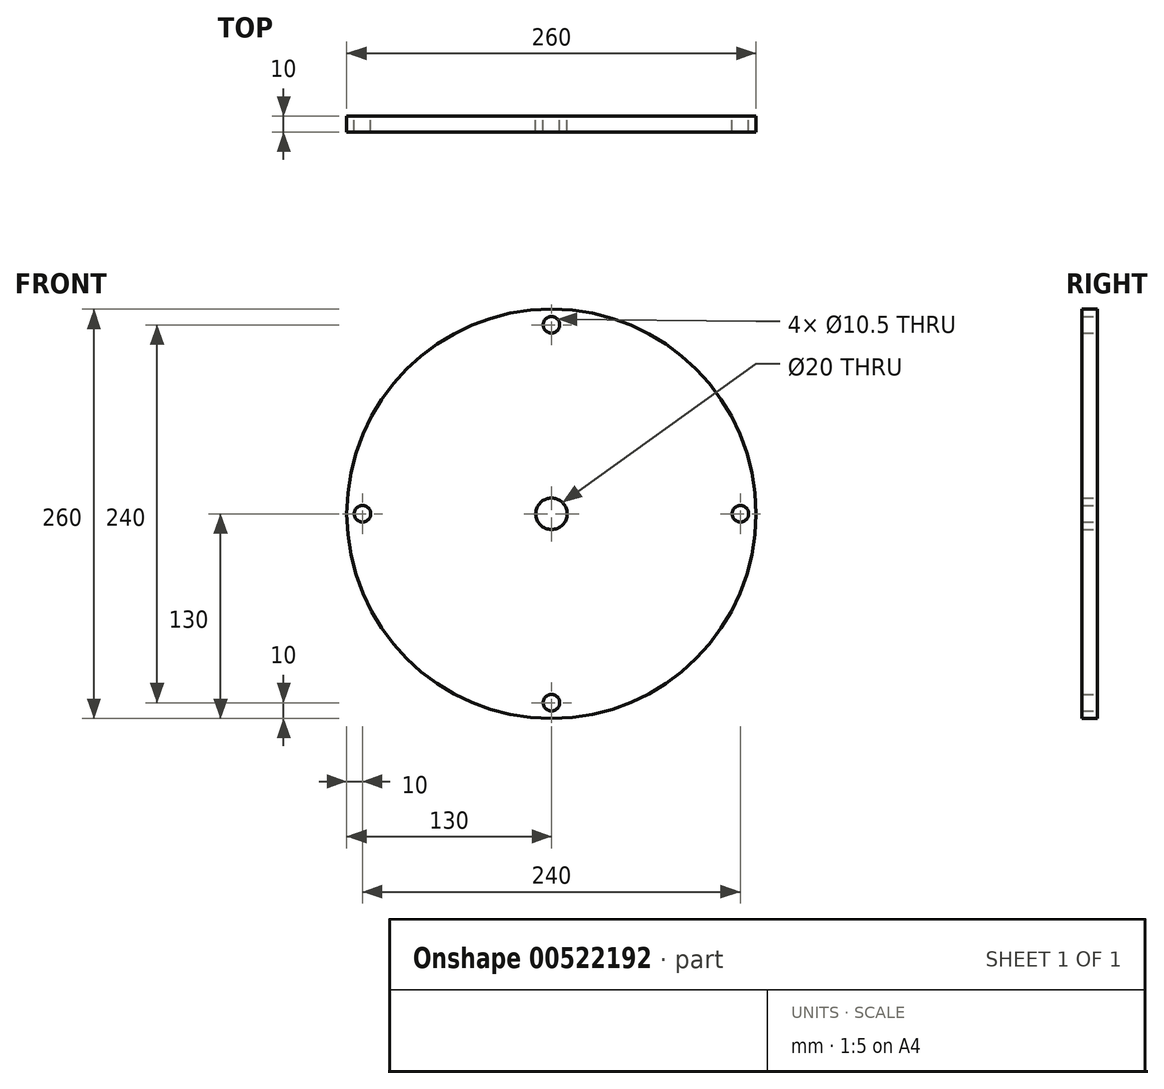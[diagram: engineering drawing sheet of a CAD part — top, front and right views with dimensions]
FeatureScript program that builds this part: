
annotation { "Feature Type Name" : "Feature", "Feature Type Description" : "" }
export const myFeature = defineFeature(function(context is Context, id is Id, definition is map)
    precondition{}
    {
        {
            var Q0;
            Q0=qCreatedBy(makeId("Front.planeOp"),FACE);
            var sketch = newSketch(context, id + "F0", { "sketchPlane" : qUnion([Q0])});
            skCircle(sketch, "E0", {"center": v(0, 0) * mm, "radius": 130 * mm});
            skCircle(sketch, "E1", {"center": v(0, 120) * mm, "radius": 5.25 * mm});
            skCircle(sketch, "E2", {"center": v(0, -120) * mm, "radius": 5.25 * mm});
            skCircle(sketch, "E3", {"center": v(120, 0) * mm, "radius": 5.25 * mm});
            skCircle(sketch, "E4", {"center": v(-120, 0) * mm, "radius": 5.25 * mm});
            skCircle(sketch, "E5", {"center": v(0, 0) * mm, "radius": 10 * mm});
            skSolve(sketch);
        }
        {
            var Q0;
            Q0=makeQuery(id+"F0.imprint","IMPRINT",FACE,{"disambiguationData":[TD([[makeQuery(id+"F0.imprint","IMPRINT",EDGE,{"derivedFrom":sQuery(id+"F0.wireOp",EDGE,"E0")}),1.0]])]});
            extrude(context, id + "F1", {"entities" : qUnion([Q0]), "depth" : 10 * mm, "offsetDistance" : 25.4 * mm});
        }
    });
